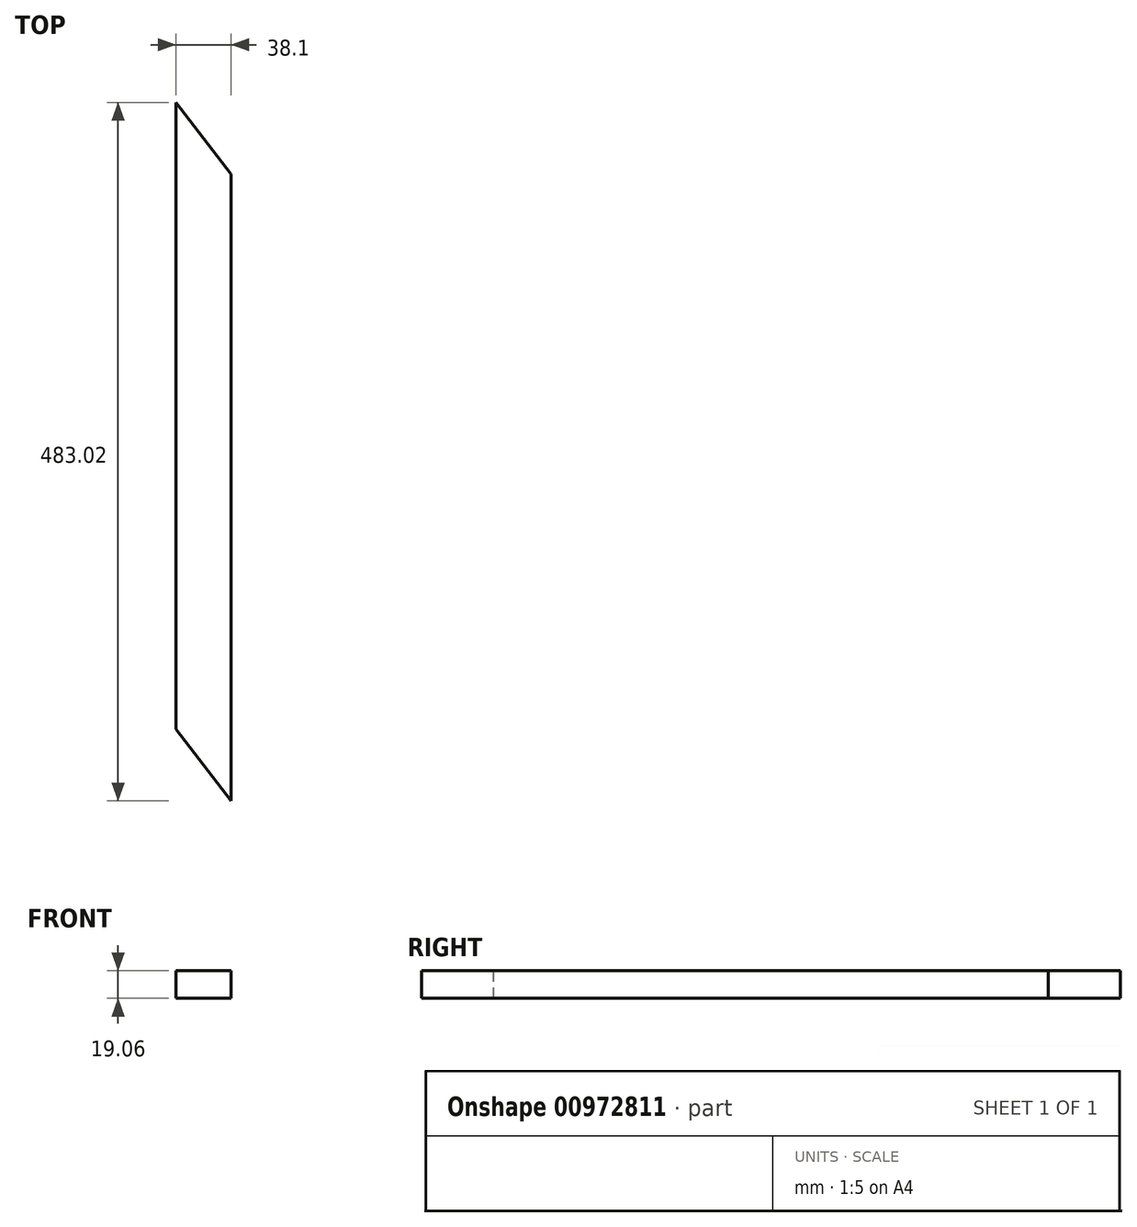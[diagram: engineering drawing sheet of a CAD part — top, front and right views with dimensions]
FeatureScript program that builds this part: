
annotation { "Feature Type Name" : "Feature", "Feature Type Description" : "" }
export const myFeature = defineFeature(function(context is Context, id is Id, definition is map)
    precondition{}
    {
        {
            var Q0;
            Q0=qCreatedBy(makeId("Front.planeOp"),FACE);
            var sketch = newSketch(context, id + "F0", { "sketchPlane" : qUnion([Q0])});
            skLineSegment(sketch, "E0.bottom", {"start": v(-19.05, 9.52) * mm, "end": v(19.05, 9.52) * mm});
            skLineSegment(sketch, "E0.top", {"start": v(-19.05, -9.52) * mm, "end": v(19.05, -9.52) * mm});
            skLineSegment(sketch, "E0.left", {"start": v(-19.05, 9.52) * mm, "end": v(-19.05, -9.52) * mm});
            skLineSegment(sketch, "E0.right", {"start": v(19.05, 9.52) * mm, "end": v(19.05, -9.52) * mm});
            skPoint(sketch, "E0.middle", {"position": v(0, 0) * mm});
            skSolve(sketch);
        }
        {
            var Q0;
            Q0=makeQuery(id+"F0.imprint","IMPRINT",FACE,{"disambiguationData":[TD([[makeQuery(id+"F0.imprint","IMPRINT",EDGE,{"derivedFrom":sQuery(id+"F0.wireOp",EDGE,"E0.bottom")}),-1.0]])]});
            extrude(context, id + "F1", {"entities" : qUnion([Q0]), "depth" : 508 * mm, "offsetDistance" : 25.4 * mm});
        }
        {
            var Q0;
            Q0=makeQuery(id+"F1.opExtrude","SWEPT_FACE",FACE,{"disambiguationData":[OSD([sQuery(id+"F0.wireOp",EDGE,"E0.bottom")])]});
            var sketch = newSketch(context, id + "F2", { "sketchPlane" : qUnion([Q0])});
            skLineSegment(sketch, "E1", {"start": v(-19.05, 0) * mm, "end": v(19.05, -49.65) * mm});
            skLineSegment(sketch, "E2", {"start": v(19.05, -49.65) * mm, "end": v(19.05, 0) * mm});
            skLineSegment(sketch, "E3", {"start": v(19.05, 0) * mm, "end": v(-19.05, 0) * mm});
            skLineSegment(sketch, "E4", {"start": v(19.05, -483.02) * mm, "end": v(-19.05, -433.37) * mm});
            skLineSegment(sketch, "E5", {"start": v(-19.05, 0) * mm, "end": v(-157.44, -106.2) * mm, "construction": true});
            skLineSegment(sketch, "E6", {"start": v(19.05, -483.02) * mm, "end": v(202.15, -342.52) * mm, "construction": true});
            skLineSegment(sketch, "E7", {"start": v(19.05, -483.02) * mm, "end": v(19.05, -508) * mm});
            skLineSegment(sketch, "E8", {"start": v(19.05, -508) * mm, "end": v(-19.05, -508) * mm});
            skLineSegment(sketch, "E9", {"start": v(-19.05, -508) * mm, "end": v(-19.05, -433.37) * mm});
            skSolve(sketch);
        }
        {
            var Q0;
            Q0=makeQuery(id+"F2.imprint","IMPRINT",FACE,{"disambiguationData":[TD([[makeQuery(id+"F2.imprint","IMPRINT",EDGE,{"derivedFrom":sQuery(id+"F2.wireOp",EDGE,"E1")}),1.0]])]});
            var Q1;
            Q1=makeQuery(id+"F2.imprint","IMPRINT",FACE,{"disambiguationData":[TD([[makeQuery(id+"F2.imprint","IMPRINT",EDGE,{"derivedFrom":sQuery(id+"F2.wireOp",EDGE,"dHMrywMa-9ylc-wSOJ-r1aX-UeNUDaHpD79S")}),1.0]])]});
            var Q2;
            Q2=makeQuery(id+"F2.imprint","IMPRINT",FACE,{"disambiguationData":[TD([[makeQuery(id+"F2.imprint","IMPRINT",EDGE,{"derivedFrom":sQuery(id+"F2.wireOp",EDGE,"E4")}),1.0]])]});
            extrude(context, id + "F3", {"entities" : qUnion([Q0, Q1, Q2]), "operationType" : NewBodyOperationType.REMOVE, "endBound" : BoundingType.THROUGH_ALL, "oppositeDirection" : true, "depth" : 25.4 * mm, "offsetDistance" : 25.4 * mm});
        }
    });
